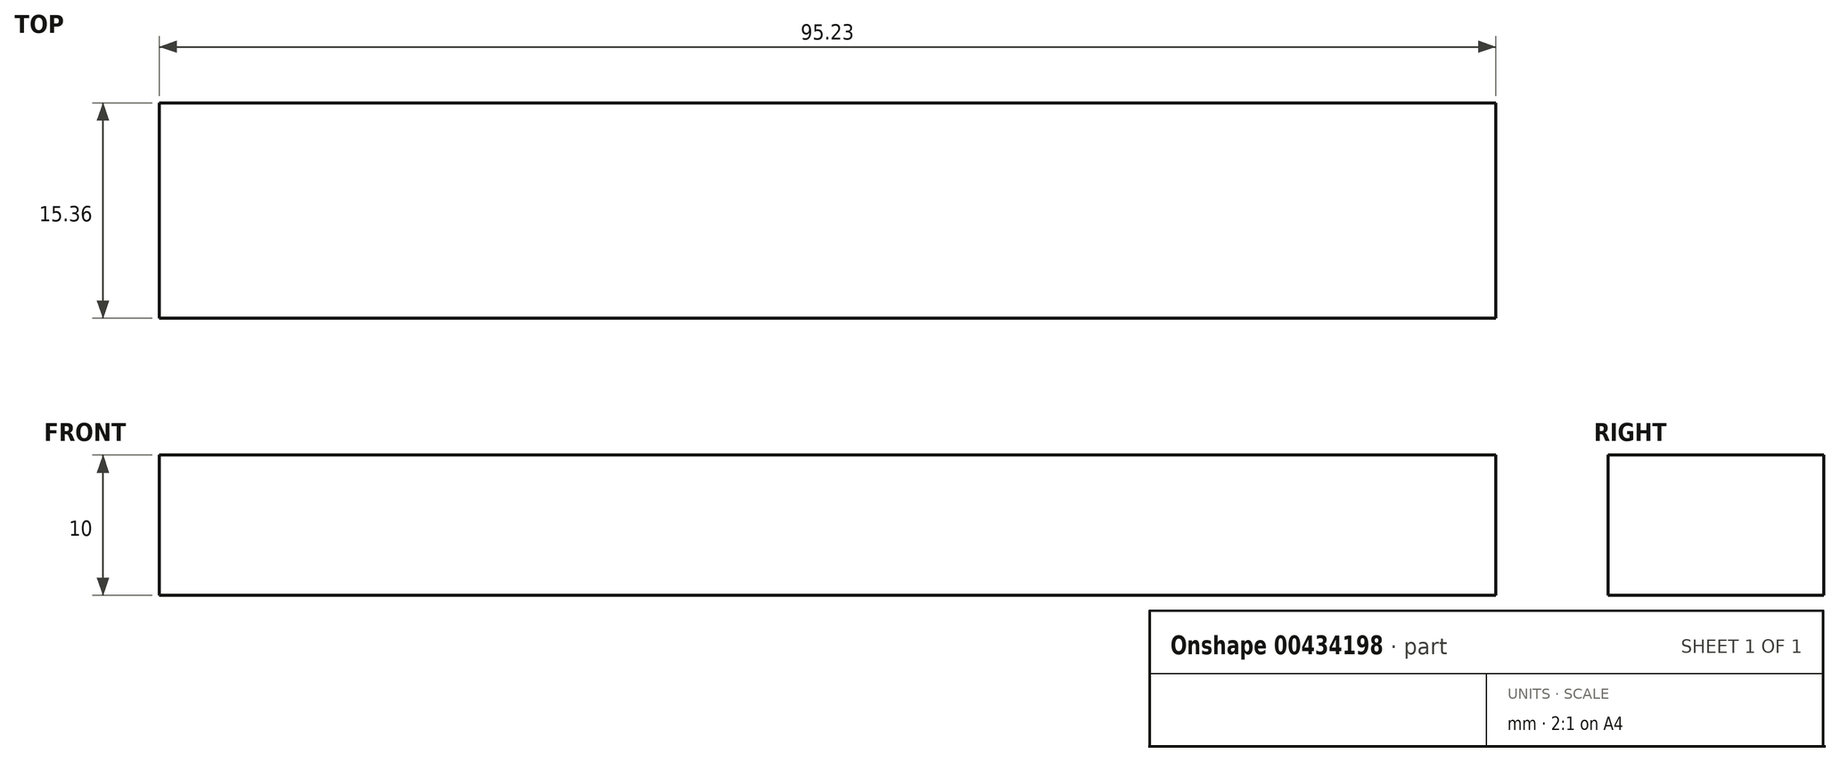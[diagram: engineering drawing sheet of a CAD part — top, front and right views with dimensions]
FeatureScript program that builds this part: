
annotation { "Feature Type Name" : "Feature", "Feature Type Description" : "" }
export const myFeature = defineFeature(function(context is Context, id is Id, definition is map)
    precondition{}
    {
        {
            var Q0;
            Q0=qCreatedBy(makeId("Top.planeOp"),FACE);
            var sketch = newSketch(context, id + "F0", { "sketchPlane" : qUnion([Q0])});
            skLineSegment(sketch, "E0.bottom", {"start": v(-118.22, -29.32) * mm, "end": v(-23, -29.32) * mm});
            skLineSegment(sketch, "E0.top", {"start": v(-118.22, -44.68) * mm, "end": v(-23, -44.68) * mm});
            skLineSegment(sketch, "E0.left", {"start": v(-118.22, -29.32) * mm, "end": v(-118.22, -44.68) * mm});
            skLineSegment(sketch, "E0.right", {"start": v(-23, -29.32) * mm, "end": v(-23, -44.68) * mm});
            skSolve(sketch);
        }
        {
            var Q0;
            Q0=makeQuery(id+"F0.imprint","IMPRINT",FACE,{"disambiguationData":[TD([[makeQuery(id+"F0.imprint","IMPRINT",EDGE,{"derivedFrom":sQuery(id+"F0.wireOp",EDGE,"E0.bottom")}),-1.0]])]});
            extrude(context, id + "F1", {"entities" : qUnion([Q0]), "depth" : 10 * mm});
        }
    });
